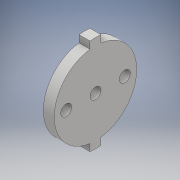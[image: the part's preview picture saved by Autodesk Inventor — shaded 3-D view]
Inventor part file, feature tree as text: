
AUTODESK INVENTOR PART (.ipt)
format: ipt  version: 2018 (Build 220112000, 112)  size: 117,760 bytes
history: native  units: mm
features: extrude x3, sketch x3, other x1
ambient origin geometry x8: Origin, YZ Plane, XZ Plane, XY Plane, X Axis, Y Axis, Z Axis, Center Point
bodies: Body1 (feature_tree)
feature tree (7):
  other  "Sólido1"
  extrude  "Extrusión1"  Depth=3.0mm TaperAngle=0.0deg
  extrude  "Extrusión2"  Depth=3.0mm
  extrude  "Extrusión3"  Depth=3.0mm
  sketch  "Boceto1"  dims[d5=22.5mm d6=3.0mm d7=0.0mm]
  sketch  "Boceto2"  dims[d14=3.0mm d15=3.0mm]
  sketch  "Boceto3"  dims[d16=3.0mm d17=0.0mm d18=3.0mm d19=10.0mm d20=0.0mm]
